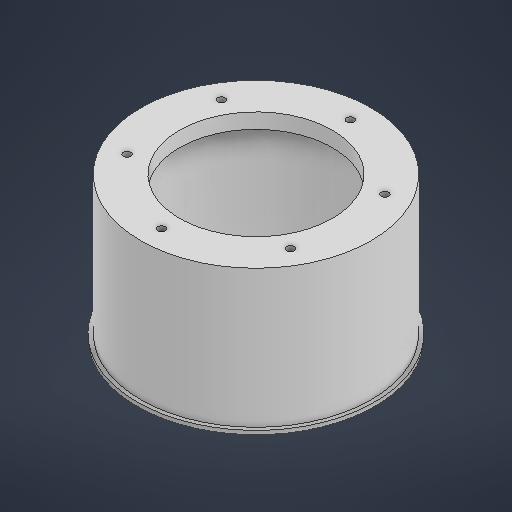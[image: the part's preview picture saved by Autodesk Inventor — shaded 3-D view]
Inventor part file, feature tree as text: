
AUTODESK INVENTOR PART (.ipt)
format: ipt  version: 2025 (Build 290162000, 162)  size: 271,360 bytes
history: native  units: in
note: dims shown in document units (in); Inventor stores cm internally (conversion verified against a paired STEP export)
features: other x12, sketch x6, extrude x5, plane x1
ambient origin geometry x8: Origin, YZ Plane, XZ Plane, XY Plane, X Axis, Y Axis, Z Axis, Center Point
bodies: Solid1 (feature_tree)
feature tree (24):
  other  "Table"
  other  "C .Replace - 01"
  other  "C .Replace - 02"
  other  "C .Replace - 03"
  other  "C .Replace - 04"
  other  "C .Replace - 05"
  other  "C .Replace - 06"
  other  "C .Replace - 07"
  other  "C .Replace - 08"
  other  "C .Replace - 09"
  other  "C .Replace - 10"
  other  "C .Replace - Face"
  sketch  "Sketch1"  dims[d5=0.0in d7=0.0in]
  extrude  "Extrusion1"  TaperAngle=0.0deg  [1 undecoded]
  extrude  "Extrusion2"  Depth=10.0394in
  extrude  "Extrusion7"  Depth=3.937in TaperAngle=360.0deg
  plane  "Work Plane2"
  extrude  "Extrusion8"  Depth=0.3937in
  extrude  "Extrusion30"  Depth=0.1575in
  sketch  "Sketch2"  dims[d28=0.1969in d29=3.937in d31=360.0deg]
  sketch  "Sketch3"  dims[d33=0.3937in d34=0.0in d52=4.5276in]
  sketch  "Sketch Circular Pattern1"  dims[d18=0.0in d27=10.0394in]
  sketch  "Sketch24"  dims[d232=2.3622in d234=360.0deg d236=0.3937in d237=0.0in d113=0.0197in d114=0.0344in d115=0.0197in d116=0.0344in d167=0.0197in d168=0.0344in d169=0.0197in d170=0.0344in d215=0.0197in d216=0.0344in d217=0.0197in d218=0.0344in d219=0.0in d220=0.0in]
  sketch  "Sketch Circular Pattern4"  dims[d230=3.937in d231=0.1575in]
note: 1 required parameter value undecoded (feature->parameter linkage not recoverable at this tier; creation-order binding heuristic only, values carry confidence <= 0.55)
